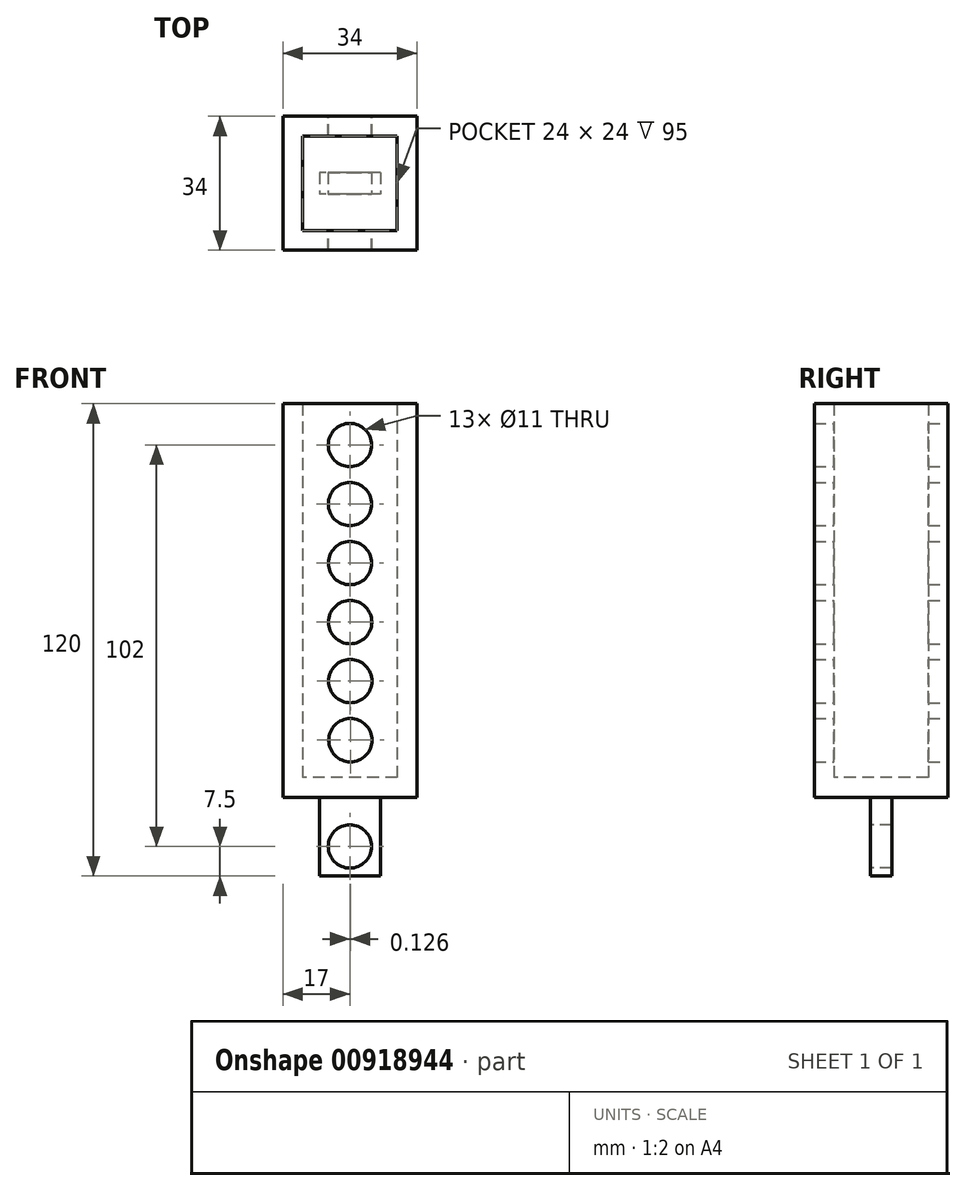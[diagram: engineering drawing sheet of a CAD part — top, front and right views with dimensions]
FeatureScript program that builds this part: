
annotation { "Feature Type Name" : "Feature", "Feature Type Description" : "" }
export const myFeature = defineFeature(function(context is Context, id is Id, definition is map)
    precondition{}
    {
        {
            var Q0;
            Q0=qCreatedBy(makeId("Top.planeOp"),FACE);
            var sketch = newSketch(context, id + "F0", { "sketchPlane" : qUnion([Q0])});
            skLineSegment(sketch, "E0.bottom", {"start": v(7.75, 2.75) * mm, "end": v(-7.75, 2.75) * mm});
            skLineSegment(sketch, "E0.top", {"start": v(7.75, -2.75) * mm, "end": v(-7.75, -2.75) * mm});
            skLineSegment(sketch, "E0.left", {"start": v(7.75, 2.75) * mm, "end": v(7.75, -2.75) * mm});
            skLineSegment(sketch, "E0.right", {"start": v(-7.75, 2.75) * mm, "end": v(-7.75, -2.75) * mm});
            skPoint(sketch, "E0.middle", {"position": v(0, 0) * mm});
            skSolve(sketch);
        }
        {
            var Q0;
            Q0 = qSketchRegion(id + "F0", true);
            extrude(context, id + "F1", {"entities" : qUnion([Q0]), "depth" : 20 * mm, "offsetDistance" : 25 * mm});
        }
        {
            var Q0;
            Q0=makeQuery(id+"F1.opExtrude","SWEPT_FACE",FACE,{"disambiguationData":[OSD([sQuery(id+"F0.wireOp",EDGE,"E0.top")])]});
            var sketch = newSketch(context, id + "F2", { "sketchPlane" : qUnion([Q0])});
            skCircle(sketch, "E1", {"center": v(0, 7.5) * mm, "radius": 5.5 * mm});
            skSolve(sketch);
        }
        {
            var Q0;
            Q0=makeQuery(id+"F2.imprint","IMPRINT",FACE,{"disambiguationData":[TD([[makeQuery(id+"F2.imprint","IMPRINT",EDGE,{"derivedFrom":sQuery(id+"F2.wireOp",EDGE,"E1")}),1.0]])]});
            extrude(context, id + "F3", {"entities" : qUnion([Q0]), "operationType" : NewBodyOperationType.REMOVE, "endBound" : BoundingType.UP_TO_NEXT, "oppositeDirection" : true, "depth" : 25 * mm, "offsetDistance" : 25 * mm});
        }
        {
            var Q0;
            Q0=makeQuery(id+"F1.opExtrude","CAP_FACE",FACE,{"disambiguationData":[OSD([sQuery(id+"F0.wireOp",EDGE,"E0.bottom"),sQuery(id+"F0.wireOp",EDGE,"E0.top"),sQuery(id+"F0.wireOp",EDGE,"E0.left"),sQuery(id+"F0.wireOp",EDGE,"E0.right")])],"isStart":false});
            var sketch = newSketch(context, id + "F4", { "sketchPlane" : qUnion([Q0])});
            skLineSegment(sketch, "E2.bottom", {"start": v(17, 17) * mm, "end": v(-17, 17) * mm});
            skLineSegment(sketch, "E2.top", {"start": v(17, -17) * mm, "end": v(-17, -17) * mm});
            skLineSegment(sketch, "E2.left", {"start": v(17, 17) * mm, "end": v(17, -17) * mm});
            skLineSegment(sketch, "E2.right", {"start": v(-17, 17) * mm, "end": v(-17, -17) * mm});
            skPoint(sketch, "E2.middle", {"position": v(0, 0) * mm});
            skSolve(sketch);
        }
        {
            var Q0;
            Q0=makeQuery(id+"F4.imprint","IMPRINT",FACE,{"disambiguationData":[TD([[makeQuery(id+"F4.imprint","IMPRINT",EDGE,{"derivedFrom":makeQuery(id+"F1.opExtrude","CAP_EDGE",EDGE,{"disambiguationData":[OSD([sQuery(id+"F0.wireOp",EDGE,"E0.bottom")])],"isStart":false})}),1.0]])]});
            var Q1;
            Q1=makeQuery(id+"F4.imprint","IMPRINT",FACE,{"disambiguationData":[TD([[makeQuery(id+"F4.imprint","IMPRINT",EDGE,{"derivedFrom":sQuery(id+"F4.wireOp",EDGE,"E2.bottom")}),1.0]])]});
            extrude(context, id + "F5", {"entities" : qUnion([Q0, Q1]), "operationType" : NewBodyOperationType.ADD, "depth" : 100 * mm, "offsetDistance" : 25 * mm});
        }
        {
            var Q0;
            Q0=makeQuery(id+"F5.opExtrude","CAP_FACE",FACE,{"disambiguationData":[OSD([sQuery(id+"F4.wireOp",EDGE,"E2.bottom"),sQuery(id+"F4.wireOp",EDGE,"E2.top"),sQuery(id+"F4.wireOp",EDGE,"E2.left"),sQuery(id+"F4.wireOp",EDGE,"E2.right")])],"isStart":false});
            shell(context, id + "F6", {"entities" : qUnion([Q0]), "thickness" : 5 * mm});
        }
        {
            var Q0;
            Q0=makeQuery(id+"F5.opExtrude","SWEPT_FACE",FACE,{"disambiguationData":[OSD([sQuery(id+"F4.wireOp",EDGE,"E2.bottom")])]});
            var sketch = newSketch(context, id + "F7", { "sketchPlane" : qUnion([Q0])});
            skCircle(sketch, "E3", {"center": v(0, 109.5) * mm, "radius": 5.5 * mm});
            skCircle(sketch, "E4.1.0.0", {"center": v(-0.03, 94.5) * mm, "radius": 5.5 * mm});
            skCircle(sketch, "E4.2.0.0", {"center": v(-0.05, 79.5) * mm, "radius": 5.5 * mm});
            skLineSegment(sketch, "E4.direction1", {"start": v(0, 109.5) * mm, "end": v(-0.03, 94.5) * mm, "construction": true});
            skCircle(sketch, "E5.0.3.0", {"center": v(-0.08, 64.5) * mm, "radius": 5.5 * mm});
            skCircle(sketch, "E5.0.4.0", {"center": v(-0.1, 49.5) * mm, "radius": 5.5 * mm});
            skCircle(sketch, "E5.0.5.0", {"center": v(-0.13, 34.5) * mm, "radius": 5.5 * mm});
            skSolve(sketch);
        }
        {
            var Q0;
            Q0=makeQuery(id+"F7.imprint","IMPRINT",FACE,{"disambiguationData":[TD([[makeQuery(id+"F7.imprint","IMPRINT",EDGE,{"derivedFrom":sQuery(id+"F7.wireOp",EDGE,"E3")}),1.0]])]});
            var Q1;
            Q1=makeQuery(id+"F7.imprint","IMPRINT",FACE,{"disambiguationData":[TD([[makeQuery(id+"F7.imprint","IMPRINT",EDGE,{"derivedFrom":sQuery(id+"F7.wireOp",EDGE,"E4.1.0.0")}),1.0]])]});
            var Q2;
            Q2=makeQuery(id+"F7.imprint","IMPRINT",FACE,{"disambiguationData":[TD([[makeQuery(id+"F7.imprint","IMPRINT",EDGE,{"derivedFrom":sQuery(id+"F7.wireOp",EDGE,"E4.2.0.0")}),1.0]])]});
            var Q3;
            Q3=makeQuery(id+"F7.imprint","IMPRINT",FACE,{"disambiguationData":[TD([[makeQuery(id+"F7.imprint","IMPRINT",EDGE,{"derivedFrom":sQuery(id+"F7.wireOp",EDGE,"E5.0.3.0")}),1.0]])]});
            var Q4;
            Q4=makeQuery(id+"F7.imprint","IMPRINT",FACE,{"disambiguationData":[TD([[makeQuery(id+"F7.imprint","IMPRINT",EDGE,{"derivedFrom":sQuery(id+"F7.wireOp",EDGE,"E5.0.4.0")}),1.0]])]});
            var Q5;
            Q5=makeQuery(id+"F7.imprint","IMPRINT",FACE,{"disambiguationData":[TD([[makeQuery(id+"F7.imprint","IMPRINT",EDGE,{"derivedFrom":sQuery(id+"F7.wireOp",EDGE,"E5.0.5.0")}),1.0]])]});
            var Q6;
            Q6=makeQuery(id+"F5.opExtrude","SWEPT_FACE",FACE,{"disambiguationData":[OSD([sQuery(id+"F4.wireOp",EDGE,"E2.top")])]});
            extrude(context, id + "F8", {"entities" : qUnion([Q0, Q1, Q2, Q3, Q4, Q5]), "operationType" : NewBodyOperationType.REMOVE, "endBound" : BoundingType.UP_TO_SURFACE, "oppositeDirection" : true, "depth" : 25 * mm, "endBoundEntityFace" : qUnion([Q6]), "offsetDistance" : 25 * mm});
        }
    });
